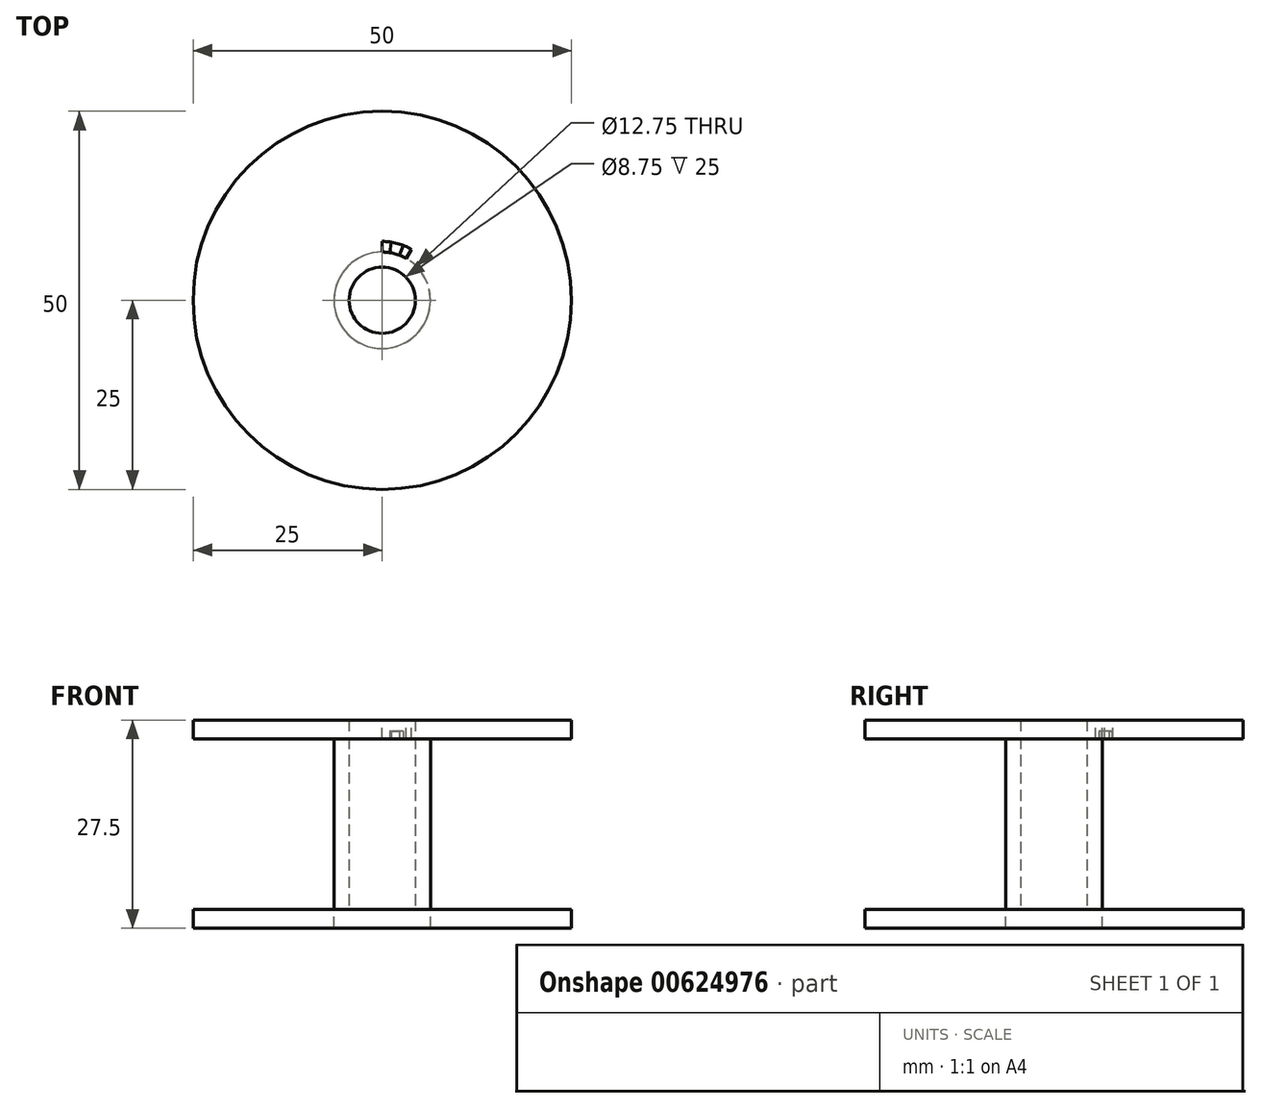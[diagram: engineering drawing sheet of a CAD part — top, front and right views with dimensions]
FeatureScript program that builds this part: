
annotation { "Feature Type Name" : "Feature", "Feature Type Description" : "" }
export const myFeature = defineFeature(function(context is Context, id is Id, definition is map)
    precondition{}
    {
        {
            var Q0;
            Q0=qCreatedBy(makeId("Top.planeOp"),FACE);
            var sketch = newSketch(context, id + "F0", { "sketchPlane" : qUnion([Q0])});
            skCircle(sketch, "E0", {"center": v(0, 0) * mm, "radius": 4.38 * mm});
            skCircle(sketch, "E1", {"center": v(0, 0) * mm, "radius": 6.38 * mm});
            skSolve(sketch);
        }
        {
            var Q0;
            Q0=makeQuery(id+"F0.imprint","IMPRINT",FACE,{"disambiguationData":[TD([[makeQuery(id+"F0.imprint","IMPRINT",EDGE,{"derivedFrom":sQuery(id+"F0.wireOp",EDGE,"E0")}),-1.0]])]});
            extrude(context, id + "F1", {"entities" : qUnion([Q0]), "endBound" : BoundingType.SYMMETRIC, "depth" : 22.5 * mm, "offsetDistance" : 25 * mm});
        }
        {
            var Q0;
            Q0=makeQuery(id+"F1.opExtrude","CAP_FACE",FACE,{"disambiguationData":[OSD([sQuery(id+"F0.wireOp",EDGE,"E0"),sQuery(id+"F0.wireOp",EDGE,"E1")])],"isStart":false});
            var sketch = newSketch(context, id + "F2", { "sketchPlane" : qUnion([Q0])});
            skCircle(sketch, "E2", {"center": v(0, 0) * mm, "radius": 25 * mm});
            skCircle(sketch, "E3.0", {"center": v(0, 0) * mm, "radius": 4.38 * mm});
            skSolve(sketch);
        }
        {
            var Q0;
            Q0=makeQuery(id+"F2.imprint","IMPRINT",FACE,{"disambiguationData":[TD([[makeQuery(id+"F2.imprint","IMPRINT",EDGE,{"derivedFrom":sQuery(id+"F2.wireOp",EDGE,"E2")}),1.0]])]});
            var Q1;
            Q1=makeQuery(id+"F2.imprint","IMPRINT",FACE,{"disambiguationData":[TD([[makeQuery(id+"F2.imprint","IMPRINT",EDGE,{"derivedFrom":sQuery(id+"F2.wireOp",EDGE,"E3.0")}),-1.0]])]});
            extrude(context, id + "F3", {"entities" : qUnion([Q0, Q1]), "operationType" : NewBodyOperationType.ADD, "depth" : 2.5 * mm, "offsetDistance" : 25 * mm});
        }
        {
            var Q0;
            Q0=makeQuery(id+"F1.opExtrude","CAP_FACE",FACE,{"disambiguationData":[OSD([sQuery(id+"F0.wireOp",EDGE,"E0"),sQuery(id+"F0.wireOp",EDGE,"E1")])],"isStart":true});
            var sketch = newSketch(context, id + "F4", { "sketchPlane" : qUnion([Q0])});
            skCircle(sketch, "E4.0", {"center": v(0, 0) * mm, "radius": 25 * mm});
            skCircle(sketch, "E5.0", {"center": v(0, 0) * mm, "radius": 4.38 * mm});
            skSolve(sketch);
        }
        {
            var Q0;
            Q0=makeQuery(id+"F3.opExtrude","CAP_FACE",FACE,{"disambiguationData":[OSD([sQuery(id+"F2.wireOp",EDGE,"E2"),sQuery(id+"F2.wireOp",EDGE,"E3.0")])],"isStart":false});
            var sketch = newSketch(context, id + "F5", { "sketchPlane" : qUnion([Q0])});
            skArc(sketch, "E6.0", {"start": v(3.19, 5.52) * mm, "mid": v(1.65, 6.16) * mm, "end": v(0, 6.38) * mm});
            skArc(sketch, "E7", {"start": v(3.89, 6.73) * mm, "mid": v(2.01, 7.51) * mm, "end": v(0, 7.78) * mm});
            skLineSegment(sketch, "E8", {"start": v(0, 6.38) * mm, "end": v(0, 7.78) * mm});
            skLineSegment(sketch, "E9", {"start": v(3.19, 5.52) * mm, "end": v(3.89, 6.73) * mm});
            skSolve(sketch);
        }
        {
            var Q0;
            Q0=makeQuery(id+"F5.imprint","IMPRINT",FACE,{"disambiguationData":[TD([[makeQuery(id+"F5.imprint","IMPRINT",EDGE,{"derivedFrom":sQuery(id+"F5.wireOp",EDGE,"E6.0")}),-1.0]])]});
            extrude(context, id + "F6", {"entities" : qUnion([Q0]), "operationType" : NewBodyOperationType.REMOVE, "endBound" : BoundingType.UP_TO_NEXT, "oppositeDirection" : true, "depth" : 25 * mm, "offsetDistance" : 25 * mm});
        }
        {
            var Q0;
            Q0=makeQuery(id+"F3.opExtrude","CAP_FACE",FACE,{"disambiguationData":[OSD([sQuery(id+"F2.wireOp",EDGE,"E2"),sQuery(id+"F2.wireOp",EDGE,"E3.0")])],"isStart":true});
            var sketch = newSketch(context, id + "F7", { "sketchPlane" : qUnion([Q0])});
            skLineSegment(sketch, "E10", {"start": v(0, 0) * mm, "end": v(2.01, -7.51) * mm, "construction": true});
            skLineSegment(sketch, "E11", {"start": v(1.2, -7.68) * mm, "end": v(0, 0) * mm});
            skLineSegment(sketch, "E12", {"start": v(2.8, -7.26) * mm, "end": v(0, 0) * mm});
            skArc(sketch, "E13.0", {"start": v(0, -7.78) * mm, "mid": v(2.01, -7.51) * mm, "end": v(3.89, -6.73) * mm});
            skArc(sketch, "E14.0", {"start": v(3.19, -5.52) * mm, "mid": v(1.65, -6.16) * mm, "end": v(0, -6.38) * mm});
            skSolve(sketch);
        }
        {
            var Q0;
            {var subQ0=sQuery(id+"F7.wireOp",EDGE,"E13.0");var subQ1=sQuery(id+"F7.wireOp",EDGE,"E11");var subQ2=makeQuery(id+"F7.imprint","INTERSECT",VERTEX,{"derivedFrom":[subQ1,subQ0]});Q0=makeQuery(id+"F7.imprint","IMPRINT",FACE,{"disambiguationData":[TD([[makeQuery(id+"F7.imprint","IMPRINT",EDGE,{"disambiguationData":[TD([[subQ2,-1.0]])],"derivedFrom":subQ1}),-1.0]])]});}
            extrude(context, id + "F8", {"entities" : qUnion([Q0]), "operationType" : NewBodyOperationType.ADD, "oppositeDirection" : true, "depth" : 1 * mm, "offsetDistance" : 25 * mm});
        }
        {
            var Q0;
            Q0=makeQuery(id+"F4.imprint","IMPRINT",FACE,{"disambiguationData":[TD([[makeQuery(id+"F4.imprint","IMPRINT",EDGE,{"derivedFrom":sQuery(id+"F4.wireOp",EDGE,"E4.0")}),1.0]])]});
            extrude(context, id + "F9", {"entities" : qUnion([Q0]), "depth" : 2.5 * mm, "offsetDistance" : 25 * mm});
        }
    });
